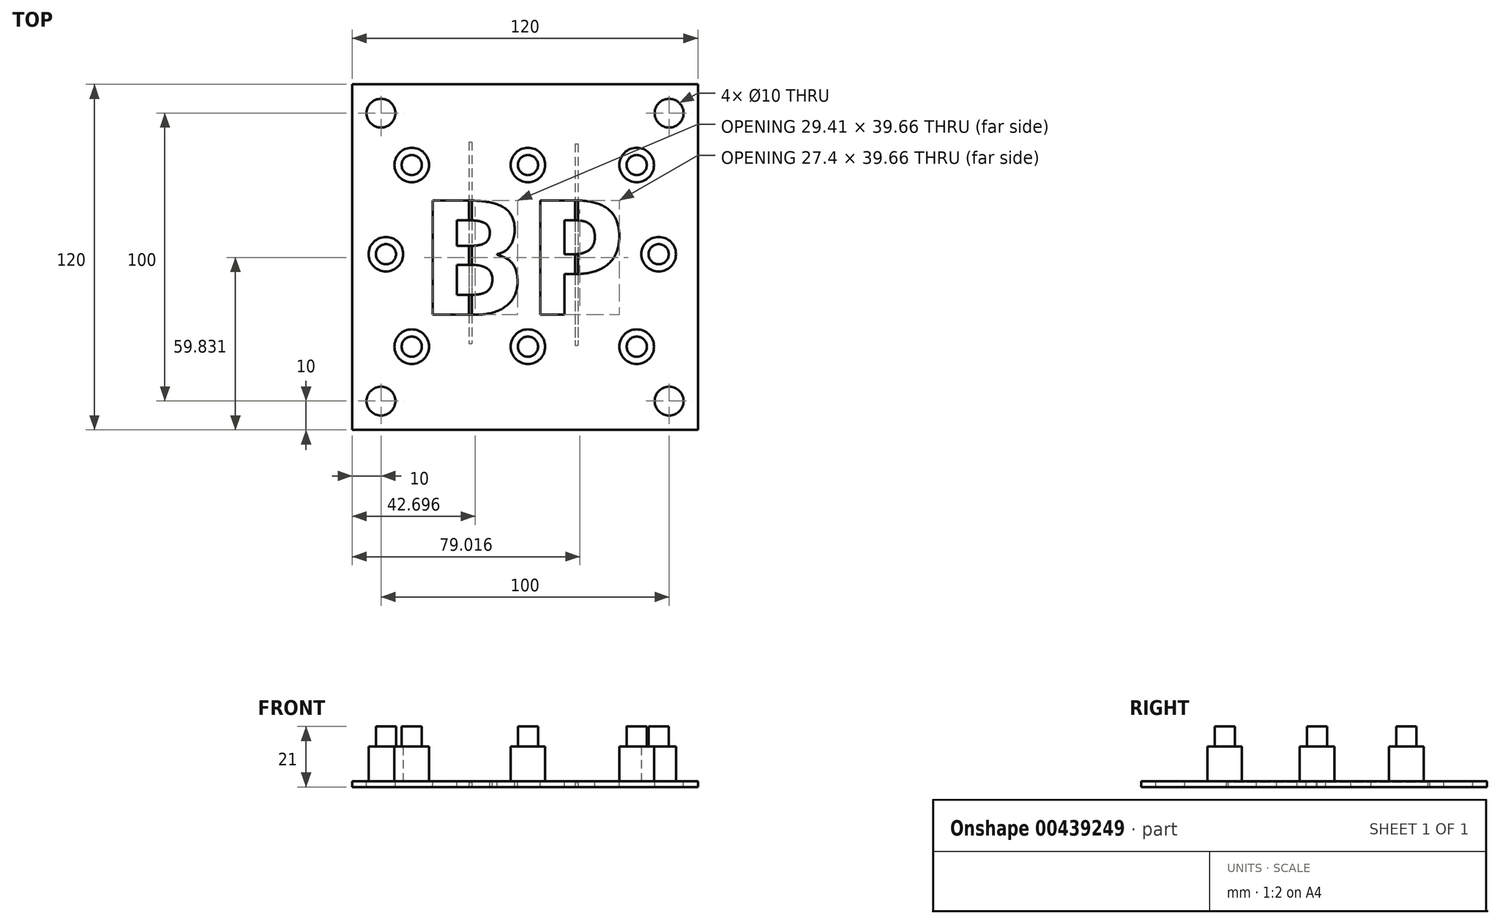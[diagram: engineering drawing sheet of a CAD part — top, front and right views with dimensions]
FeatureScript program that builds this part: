
annotation { "Feature Type Name" : "Feature", "Feature Type Description" : "" }
export const myFeature = defineFeature(function(context is Context, id is Id, definition is map)
    precondition{}
    {
        {
            var Q0;
            Q0=qCreatedBy(makeId("Top.planeOp"),FACE);
            var sketch = newSketch(context, id + "F0", { "sketchPlane" : qUnion([Q0])});
            skLineSegment(sketch, "E0.bottom", {"start": v(-61, 60) * mm, "end": v(59, 60) * mm});
            skLineSegment(sketch, "E0.top", {"start": v(-61, -60) * mm, "end": v(59, -60) * mm});
            skLineSegment(sketch, "E0.left", {"start": v(-61, 60) * mm, "end": v(-61, -60) * mm});
            skLineSegment(sketch, "E0.right", {"start": v(59, 60) * mm, "end": v(59, -60) * mm});
            skSolve(sketch);
        }
        {
            var Q0;
            Q0=qSketchRegion(id+"F0",true);
            extrude(context, id + "F1", {"entities" : qUnion([Q0]), "depth" : 2 * mm});
        }
        {
            var Q0;
            Q0=makeQuery(id+"F1.opExtrude","CAP_FACE",FACE,{"disambiguationData":[OSD([sQuery(id+"F0.wireOp",EDGE,"E0.bottom"),sQuery(id+"F0.wireOp",EDGE,"E0.top"),sQuery(id+"F0.wireOp",EDGE,"E0.left"),sQuery(id+"F0.wireOp",EDGE,"E0.right")])],"isStart":false});
            var sketch = newSketch(context, id + "F2", { "sketchPlane" : qUnion([Q0])});
            skText(sketch, "E1", { "text": "BP\n", "fontName": "OpenSans-Bold.ttf"});
            skCircle(sketch, "E2", {"center": v(-51, -50) * mm, "radius": 5 * mm});
            skCircle(sketch, "E3", {"center": v(-51, 50) * mm, "radius": 5 * mm});
            skCircle(sketch, "E4", {"center": v(49, 50) * mm, "radius": 5 * mm});
            skCircle(sketch, "E5", {"center": v(49, -50) * mm, "radius": 5 * mm});
            const initialGuessF2  = {"E1": [-0.038, -0.02, 1, 0, 0.04]};
            skSetInitialGuess(sketch, initialGuessF2);
            skSolve(sketch);
        }
        {
            var Q0;
            Q0=qSketchRegion(id+"F2",true);
            extrude(context, id + "F3", {"entities" : qUnion([Q0]), "operationType" : NewBodyOperationType.REMOVE, "oppositeDirection" : true, "depth" : 25 * mm});
        }
        {
            var Q0;
            {var subQ0=sQuery(id+"F0.wireOp",EDGE,"E0.top");var subQ1=sQuery(id+"F0.wireOp",EDGE,"E0.right");var subQ2=sQuery(id+"F0.wireOp",EDGE,"E0.bottom");var subQ3=sQuery(id+"F0.wireOp",EDGE,"E0.left");Q0=makeQuery(id+"F3.boolean.opBoolean","SPLIT",FACE,{"disambiguationData":[TD([makeQuery(id+"F1.opExtrude","SWEPT_FACE",FACE,{"disambiguationData":[OSD([subQ2])]})])],"derivedFrom":makeQuery(id+"F1.opExtrude","CAP_FACE",FACE,{"disambiguationData":[OSD([subQ2,subQ0,subQ3,subQ1])],"isStart":false})});}
            var sketch = newSketch(context, id + "F4", { "sketchPlane" : qUnion([Q0])});
            skCircle(sketch, "E6", {"center": v(-40.32, -31.09) * mm, "radius": 6 * mm});
            skCircle(sketch, "E7", {"center": v(0, -31.09) * mm, "radius": 6 * mm});
            skCircle(sketch, "E8", {"center": v(37.75, -31.09) * mm, "radius": 6 * mm});
            skCircle(sketch, "E9", {"center": v(-40.32, 31.98) * mm, "radius": 6 * mm});
            skCircle(sketch, "E10", {"center": v(0, 31.98) * mm, "radius": 6 * mm});
            skCircle(sketch, "E11", {"center": v(37.75, 31.98) * mm, "radius": 6 * mm});
            skCircle(sketch, "E12", {"center": v(-49.3, 1) * mm, "radius": 6 * mm});
            skCircle(sketch, "E13", {"center": v(45.37, 1) * mm, "radius": 6 * mm});
            skSolve(sketch);
        }
        {
            var Q0;
            {var subQ0=sQuery(id+"F0.wireOp",EDGE,"E0.top");var subQ1=sQuery(id+"F0.wireOp",EDGE,"E0.right");var subQ2=sQuery(id+"F0.wireOp",EDGE,"E0.bottom");var subQ3=sQuery(id+"F0.wireOp",EDGE,"E0.left");Q0=makeQuery(id+"F3.boolean.opBoolean","SPLIT",FACE,{"disambiguationData":[TD([makeQuery(id+"F1.opExtrude","SWEPT_FACE",FACE,{"disambiguationData":[OSD([subQ2])]})])],"derivedFrom":makeQuery(id+"F1.opExtrude","CAP_FACE",FACE,{"disambiguationData":[OSD([subQ2,subQ0,subQ3,subQ1])],"isStart":false})});}
            var sketch = newSketch(context, id + "F5", { "sketchPlane" : qUnion([Q0])});
            skCircle(sketch, "E14", {"center": v(-40.32, -31.09) * mm, "radius": 3.5 * mm});
            skCircle(sketch, "E15", {"center": v(0, -31.09) * mm, "radius": 3.5 * mm});
            skCircle(sketch, "E16", {"center": v(37.76, -31.09) * mm, "radius": 3.5 * mm});
            skCircle(sketch, "E17", {"center": v(-40.32, 31.98) * mm, "radius": 3.5 * mm});
            skCircle(sketch, "E18", {"center": v(0, 31.98) * mm, "radius": 3.5 * mm});
            skCircle(sketch, "E19", {"center": v(37.75, 31.98) * mm, "radius": 3.5 * mm});
            skCircle(sketch, "E20", {"center": v(-49.28, 1) * mm, "radius": 3.5 * mm});
            skCircle(sketch, "E21", {"center": v(45.37, 1) * mm, "radius": 3.5 * mm});
            skSolve(sketch);
        }
        {
            var Q0;
            Q0 = qSketchRegion(id + "F4", true);
            extrude(context, id + "F6", {"entities" : qUnion([Q0]), "operationType" : NewBodyOperationType.ADD, "depth" : 12 * mm});
        }
        {
            var Q0;
            Q0 = qSketchRegion(id + "F5", true);
            extrude(context, id + "F7", {"entities" : qUnion([Q0]), "operationType" : NewBodyOperationType.ADD, "depth" : 19 * mm});
        }
        {
            var Q0;
            Q0=qCreatedBy(makeId("Top.planeOp"),FACE);
            var sketch = newSketch(context, id + "F8", { "sketchPlane" : qUnion([Q0])});
            skLineSegment(sketch, "E22.bottom", {"start": v(-20.44, 40) * mm, "end": v(-19.44, 40) * mm});
            skLineSegment(sketch, "E22.top", {"start": v(-20.44, -30) * mm, "end": v(-19.44, -30) * mm});
            skLineSegment(sketch, "E22.left", {"start": v(-20.44, 40) * mm, "end": v(-20.44, -30) * mm});
            skLineSegment(sketch, "E22.right", {"start": v(-19.44, 40) * mm, "end": v(-19.44, -30) * mm});
            skLineSegment(sketch, "E23.bottom", {"start": v(16.31, 39.38) * mm, "end": v(17.31, 39.38) * mm});
            skLineSegment(sketch, "E23.top", {"start": v(16.31, -30.62) * mm, "end": v(17.31, -30.62) * mm});
            skLineSegment(sketch, "E23.left", {"start": v(16.31, 39.38) * mm, "end": v(16.31, -30.62) * mm});
            skLineSegment(sketch, "E23.right", {"start": v(17.31, 39.38) * mm, "end": v(17.31, -30.62) * mm});
            skSolve(sketch);
        }
        {
            var Q0;
            Q0 = qSketchRegion(id + "F8", true);
            extrude(context, id + "F9", {"entities" : qUnion([Q0]), "depth" : 1.6 * mm});
        }
    });
